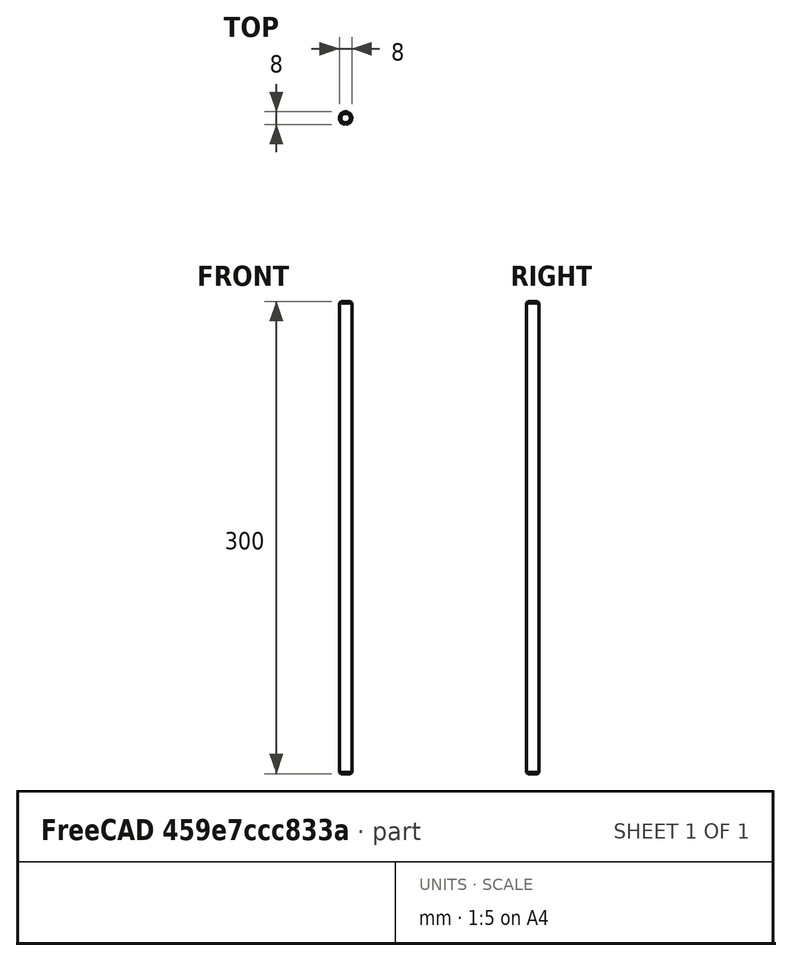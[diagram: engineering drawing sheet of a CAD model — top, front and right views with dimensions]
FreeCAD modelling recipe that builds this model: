
FCSTD DOCUMENT  (FreeCAD 0.17R13519 (Git))
Label: Corelia_Leadscrew
License: All rights reserved
LicenseURL: http://en.wikipedia.org/wiki/All_rights_reserved
objects: Sketcher::SketchObject×1, PartDesign::Pad×1, PartDesign::Chamfer×1, PartDesign::Body×1
note: 5 computed .brp shape members not serialized (recipe doc carries the construction recipe); baked Part::Feature solids carry a one-line shape summary decoded from their .brp

FEATURE [Sketcher::SketchObject] Sketch
  MapMode = 5
  Support = -> [XY_Plane]
  sketch-geometry (1):
    g0: Circle CenterX=0 CenterY=0 CenterZ=0 NormalX=0 NormalY=0 NormalZ=1 AngleXU=0 Radius=4
  constraints (2):
    c: Coincident(g0,g-1)
    c: Radius(g0) = 4
FEATURE [PartDesign::Pad] Pad
  Length = 300
  Length2 = 100
  Profile = -> Sketch
  Type = 0
FEATURE [PartDesign::Chamfer] Chamfer
  Base = -> Pad [Edge3,Edge2]
  BaseFeature = -> Pad
  Size = 1
FEATURE [PartDesign::Body] Body
  Group = -> [Sketch,Pad,Chamfer]
  Origin = -> Origin
  Tip = -> Chamfer
